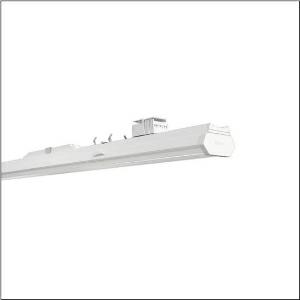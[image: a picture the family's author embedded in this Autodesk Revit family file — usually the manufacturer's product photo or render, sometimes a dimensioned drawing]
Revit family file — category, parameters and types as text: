
# Revit family: licross_21_protected_ho_52td12dn4e5m3s
name_source: partatom
category: Lighting Fixtures
units: mm (PartAtom-declared; Revit-internal decimal feet)

## family parameters
Cut with Voids When Loaded = No
Host = Face
Light Source = No
Part Type = Normal
Room Calculation Point = No
Round Connector Dimension = Use Diameter
Shared = No

## types (1)
- --- (1 x LED, 910 lm, 7.6 W, 4000K)
    Apparent Load = 8 VA
    CIE Flux Codes = 70 91 97 98 100
    Color Rendering = 80
    Color Temperature = 4000K
    Default Elevation = 1800 mm
    Description = Licross 21 Protected HO, luminaire insert, of sheet steel, galvanised, coil coated, white, length: 1.500mm, width: 90mm, height: 103mm, LED rated luminous flux: 14.690lm, light colour: 840, SDCM (Standard Deviation of Colour Matching)MacAdam ≤ 3 SDCM (initial), control gear: DALI 2 (for two DALI lines), with plug, 6-pole, with phase selection, for trunking rail, 14-core, mains connection: 220..240V, AC, 50/60Hz, rated input power: 89W, for trunking rail, 14-core, internal wiring halogen-free, for emergency light function, converter,control gear: single battery element, battery: LiFePO4, 9Ah, primary light control with lens, of plastic, primary optical cover: cover, of PMMA, light emission: direct distribution, primary light characteristic: symmetric, protection rating (complete): IP54, insulation class (complete): insulation class I (protective earthing), certification: CE, UKCA, protection symbol: D if used in an environment with non-conductive dust loads with corresponding accessories, impact resistance: IK06, permissible ambient temperature for indoor applications: +5..+30°C, standard: EN 60598-2-22, LABS conformity tested according to VDMA 24364:2018-05, reducing of maximum allowable ambient temperature of 5°C with ceiling mounting, corresponds to IFS (International Featured Standards) requirements for safety and quality in the food industry, The light source and the operating device comply with the requirements of the Ecodesign Regulation (EU) 2019/2020 and are replaceable in accordance with this regulation, packaging unit: 1 piece
    Height = 92 mm
    Lamp = 1 x LED
    Lamp Light Flux = 910 lm
    Lamp Power = 7.6 W
    Lamp count = 1
    Length = 1500 mm
    Luminous efficacy = 120 lm/W
    Manufacturer = Siteco
    ModVariant = No
    Model = 52TD12DN4E5M3S
    Mounting Place = Ceiling
    Mounting Type = Pendant
    Number of Poles = 1
    OnlyDefault = Yes
    Power Factor = 1
    Product Name = Licross 21 Protected HO
    Product group = luminaire insert | ceiling pendant
    ProductGroupID = 901
    Protection Class = Protection class I
    Protection Degree = IP 54
    RLX_Detail_Level = 1
    RLX_Emergency_Light_Flux = 0 lm
    RLX_Emergency_Type = 0
    RLX_Emergency_Type_DB = No
    RlxData = <blob elided: 25181 chars, md5=ae84f5d6>
    Socket = socket
    Standby Power = 0 W
    System Light Flux = 910 lm
    System Power = 8 W
    Type Comments = : emergency light operation: 3 h
    Type Image = l_1256148.jpg
    URL = http://relux.com
    VarID = @adj_111179
    Voltage = 0 V
    Weight = 0.00 kg
    Width = 88 mm

## geometry (parser evidence)
native form markers: Blend x4, Sweep x11
no freeform markers — native parametric forms only
